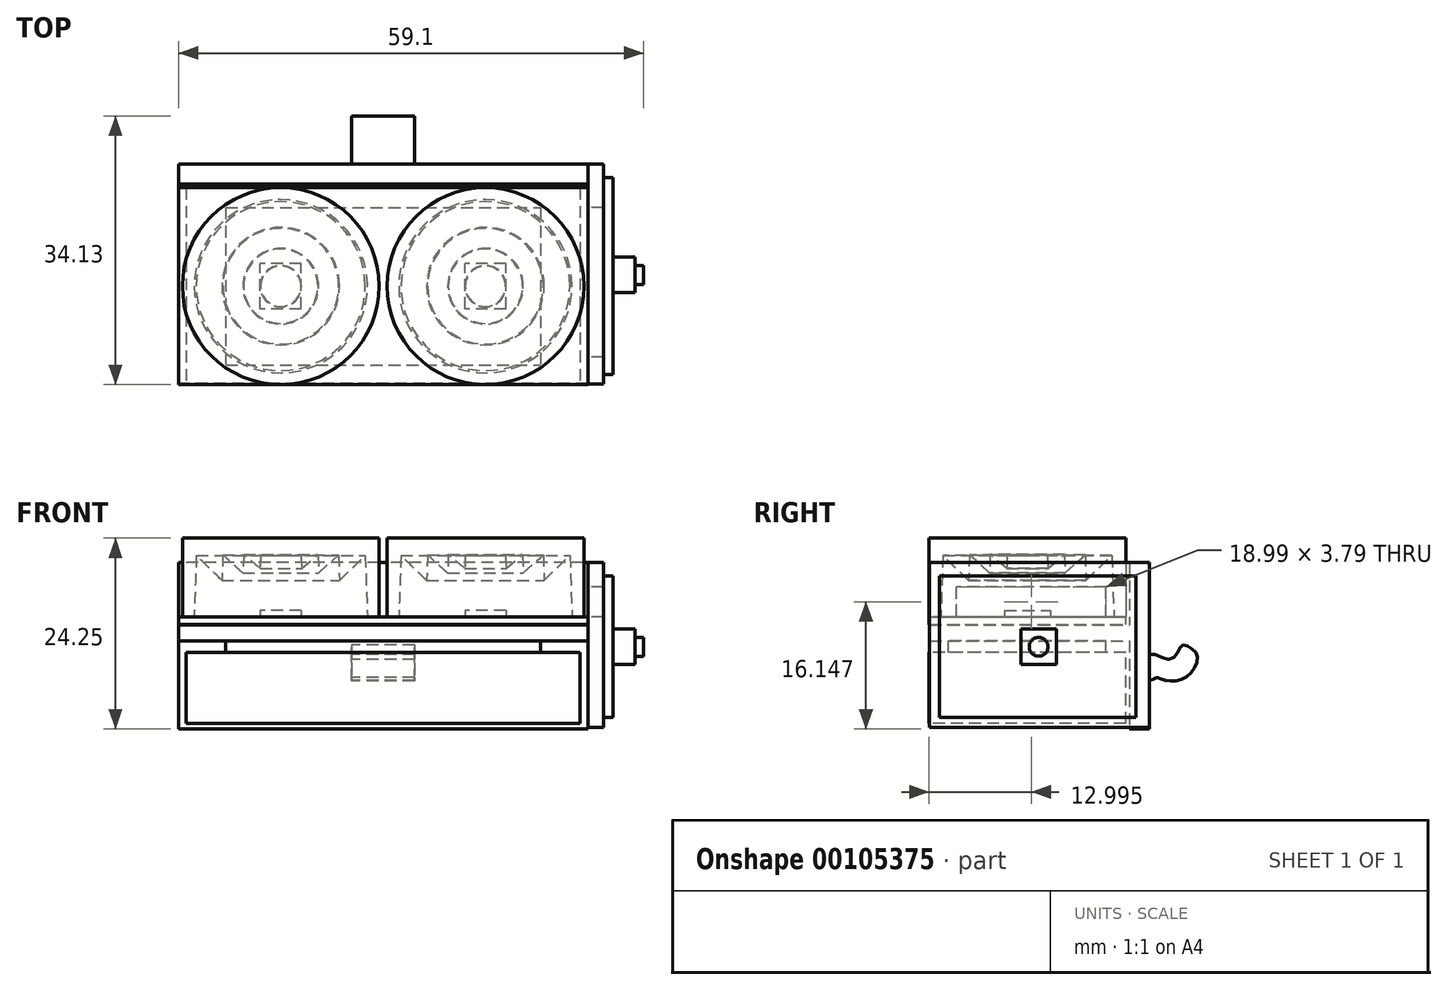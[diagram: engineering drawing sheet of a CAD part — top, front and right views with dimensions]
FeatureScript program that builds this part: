
annotation { "Feature Type Name" : "Feature", "Feature Type Description" : "" }
export const myFeature = defineFeature(function(context is Context, id is Id, definition is map)
    precondition{}
    {
        {
            var Q0;
            Q0=qCreatedBy(makeId("Top.planeOp"),FACE);
            var sketch = newSketch(context, id + "F0", { "sketchPlane" : qUnion([Q0])});
            skLineSegment(sketch, "E0.bottom", {"start": v(26, -12.5) * mm, "end": v(-26, -12.5) * mm});
            skLineSegment(sketch, "E0.top", {"start": v(26, 12.5) * mm, "end": v(-26, 12.5) * mm});
            skLineSegment(sketch, "E0.left", {"start": v(26, -12.5) * mm, "end": v(26, 12.5) * mm});
            skLineSegment(sketch, "E0.right", {"start": v(-26, -12.5) * mm, "end": v(-26, 12.5) * mm});
            skPoint(sketch, "E0.middle", {"position": v(0, 0) * mm});
            skLineSegment(sketch, "E1", {"start": v(-26, 0) * mm, "end": v(26, 0) * mm, "construction": true});
            skLineSegment(sketch, "E2", {"start": v(0, 12.5) * mm, "end": v(0, -12.5) * mm, "construction": true});
            skLineSegment(sketch, "E3", {"start": v(13, 12.5) * mm, "end": v(13, -12.5) * mm, "construction": true});
            skLineSegment(sketch, "E4", {"start": v(-13, 12.5) * mm, "end": v(-13, -12.5) * mm, "construction": true});
            skSolve(sketch);
        }
        {
            var Q0;
            Q0=qCreatedBy(makeId("Front.planeOp"),FACE);
            var sketch = newSketch(context, id + "F1", { "sketchPlane" : qUnion([Q0])});
            skLineSegment(sketch, "E5", {"start": v(13, 0) * mm, "end": v(13, 10) * mm, "construction": true});
            skLineSegment(sketch, "E6", {"start": v(13, 10) * mm, "end": v(25.5, 10) * mm});
            skLineSegment(sketch, "E7", {"start": v(25.5, 10) * mm, "end": v(25.5, 0) * mm});
            skLineSegment(sketch, "E8", {"start": v(25.5, 0) * mm, "end": v(24, 0) * mm});
            skLineSegment(sketch, "E9", {"start": v(24, 0) * mm, "end": v(23.73, 7.79) * mm});
            skLineSegment(sketch, "E10", {"start": v(23.73, 7.79) * mm, "end": v(20.47, 4.62) * mm});
            skLineSegment(sketch, "E11", {"start": v(20.47, 4.62) * mm, "end": v(20.35, 7.89) * mm});
            skLineSegment(sketch, "E12", {"start": v(20.35, 7.89) * mm, "end": v(17.8, 5.54) * mm});
            skLineSegment(sketch, "E13", {"start": v(17.8, 5.54) * mm, "end": v(17.72, 7.9) * mm});
            skLineSegment(sketch, "E14", {"start": v(17.72, 7.9) * mm, "end": v(15.63, 6.16) * mm});
            skLineSegment(sketch, "E15", {"start": v(15.63, 6.16) * mm, "end": v(15.57, 7.82) * mm});
            skLineSegment(sketch, "E16", {"start": v(13, 7.82) * mm, "end": v(13, 10) * mm});
            skLineSegment(sketch, "E17", {"start": v(0, 0) * mm, "end": v(13, 0) * mm, "construction": true});
            skLineSegment(sketch, "E18", {"start": v(15.57, 7.82) * mm, "end": v(13, 7.82) * mm});
            skSolve(sketch);
        }
        {
            var Q0;
            Q0 = qSketchRegion(id + "F1", true);
            var Q1;
            Q1=sQuery(id+"F1.wireOp",EDGE,"E5");
            revolve(context, id + "F2", {"entities" : qUnion([Q0]), "axis" : qUnion([Q1]), "revolveType" : RevolveType.FULL});
        }
        {
            var Q0;
            Q0=qCreatedBy(makeId("Top.planeOp"),FACE);
            var sketch = newSketch(context, id + "F3", { "sketchPlane" : qUnion([Q0])});
            skLineSegment(sketch, "E19.bottom", {"start": v(15.6, -2.9) * mm, "end": v(10.4, -2.9) * mm});
            skLineSegment(sketch, "E19.top", {"start": v(15.6, 2.9) * mm, "end": v(10.4, 2.9) * mm});
            skLineSegment(sketch, "E19.left", {"start": v(15.6, -2.9) * mm, "end": v(15.6, 2.9) * mm});
            skLineSegment(sketch, "E19.right", {"start": v(10.4, -2.9) * mm, "end": v(10.4, 2.9) * mm});
            skPoint(sketch, "E19.middle", {"position": v(13, 0) * mm});
            skSolve(sketch);
        }
        {
            var Q0;
            Q0 = qSketchRegion(id + "F3", true);
            extrude(context, id + "F4", {"entities" : qUnion([Q0]), "depth" : 0.8 * mm});
        }
        {
            var Q0;
            Q0 = qSketchRegion(id + "F0", true);
            extrude(context, id + "F5", {"entities" : qUnion([Q0]), "oppositeDirection" : true, "depth" : 1 * mm});
        }
        {
            var Q0;
            Q0=qCreatedBy(makeId("Right.planeOp"),FACE);
            var sketch = newSketch(context, id + "F6", { "sketchPlane" : qUnion([Q0])});
            skLineSegment(sketch, "E20.bottom", {"start": v(-12.4, -1.05) * mm, "end": v(12.96, -1.05) * mm});
            skLineSegment(sketch, "E20.top", {"start": v(-12.4, -3.05) * mm, "end": v(12.96, -3.05) * mm});
            skLineSegment(sketch, "E20.left", {"start": v(-12.4, -1.05) * mm, "end": v(-12.4, -3.05) * mm});
            skLineSegment(sketch, "E21.bottom", {"start": v(12.96, 6.9) * mm, "end": v(15.52, 6.9) * mm});
            skLineSegment(sketch, "E21.top", {"start": v(12.96, -14.25) * mm, "end": v(15.52, -14.25) * mm});
            skLineSegment(sketch, "E21.left", {"start": v(12.96, 6.9) * mm, "end": v(12.96, -1.05) * mm});
            skLineSegment(sketch, "E21.right", {"start": v(15.52, 6.9) * mm, "end": v(15.52, -4.8) * mm});
            skLineSegment(sketch, "E22.trimOffspring", {"start": v(12.96, -3.05) * mm, "end": v(12.96, -14.25) * mm});
            skFitSpline(sketch, "E23", {"points": [v(15.52, -4.8) * mm, v(17.62, -5.37) * mm, v(19.02, -4.67) * mm, v(19.65, -3.62) * mm, v(20.77, -3.97) * mm, v(21.6, -4.95) * mm, v(21.19, -6.55) * mm, v(19.93, -7.81) * mm, v(18.4, -8.16) * mm, v(17.13, -7.95) * mm, v(16.23, -7.74) * mm, v(15.52, -8.1) * mm, v(15.52, -4.8) * mm]});
            skLineSegment(sketch, "E24.trimOffspring", {"start": v(15.52, -8.1) * mm, "end": v(15.52, -14.25) * mm});
            skSolve(sketch);
        }
        {
            var Q0;
            Q0 = qSketchRegion(id + "F6", true);
            extrude(context, id + "F7", {"entities" : qUnion([Q0]), "endBound" : BoundingType.SYMMETRIC, "depth" : 52 * mm});
        }
        {
            var Q0;
            Q0=makeQuery(id+"F7.opExtrude","SWEPT_FACE",FACE,{"disambiguationData":[OSD([sQuery(id+"F6.wireOp",EDGE,"E21.bottom")])]});
            var sketch = newSketch(context, id + "F8", { "sketchPlane" : qUnion([Q0])});
            skLineSegment(sketch, "E25.bottom", {"start": v(26, 15.52) * mm, "end": v(4, 15.52) * mm});
            skLineSegment(sketch, "E25.top", {"start": v(26, 22.23) * mm, "end": v(4, 22.23) * mm});
            skLineSegment(sketch, "E25.left", {"start": v(26, 15.52) * mm, "end": v(26, 22.23) * mm});
            skLineSegment(sketch, "E25.right", {"start": v(4, 15.52) * mm, "end": v(4, 22.23) * mm});
            skLineSegment(sketch, "E26.bottom", {"start": v(-26, 15.52) * mm, "end": v(-4, 15.52) * mm});
            skLineSegment(sketch, "E26.top", {"start": v(-26, 22.17) * mm, "end": v(-4, 22.17) * mm});
            skLineSegment(sketch, "E26.left", {"start": v(-26, 15.52) * mm, "end": v(-26, 22.17) * mm});
            skLineSegment(sketch, "E26.right", {"start": v(-4, 15.52) * mm, "end": v(-4, 22.17) * mm});
            skSolve(sketch);
        }
        {
            var Q0;
            Q0 = qSketchRegion(id + "F8", true);
            extrude(context, id + "F9", {"entities" : qUnion([Q0]), "operationType" : NewBodyOperationType.REMOVE, "oppositeDirection" : true, "depth" : 25 * mm});
        }
        {
            var Q0;
            Q0=makeQuery(id+"F7.opExtrude","SWEPT_FACE",FACE,{"disambiguationData":[OSD([sQuery(id+"F6.wireOp",EDGE,"E20.top")])]});
            var sketch = newSketch(context, id + "F10", { "sketchPlane" : qUnion([Q0])});
            skLineSegment(sketch, "E27.bottom", {"start": v(-20, -10) * mm, "end": v(20, -10) * mm});
            skLineSegment(sketch, "E27.top", {"start": v(-20, 10) * mm, "end": v(20, 10) * mm});
            skLineSegment(sketch, "E27.left", {"start": v(-20, -10) * mm, "end": v(-20, 10) * mm});
            skLineSegment(sketch, "E27.right", {"start": v(20, -10) * mm, "end": v(20, 10) * mm});
            skPoint(sketch, "E27.middle", {"position": v(0, 0) * mm});
            skSolve(sketch);
        }
        {
            var Q0;
            Q0 = qSketchRegion(id + "F10", true);
            extrude(context, id + "F11", {"entities" : qUnion([Q0]), "depth" : 1.5 * mm});
        }
        {
            var Q0;
            Q0=makeQuery(id+"F11.opExtrude","CAP_FACE",FACE,{"disambiguationData":[OSD([sQuery(id+"F10.wireOp",EDGE,"E27.bottom"),sQuery(id+"F10.wireOp",EDGE,"E27.top"),sQuery(id+"F10.wireOp",EDGE,"E27.left"),sQuery(id+"F10.wireOp",EDGE,"E27.right")])],"isStart":false});
            var sketch = newSketch(context, id + "F12", { "sketchPlane" : qUnion([Q0])});
            skLineSegment(sketch, "E28.bottom", {"start": v(-25, -12.5) * mm, "end": v(25, -12.5) * mm});
            skLineSegment(sketch, "E28.top", {"start": v(-25, 12.5) * mm, "end": v(25, 12.5) * mm});
            skLineSegment(sketch, "E28.left", {"start": v(-25, -12.5) * mm, "end": v(-25, 12.5) * mm});
            skLineSegment(sketch, "E28.right", {"start": v(25, -12.5) * mm, "end": v(25, 12.5) * mm});
            skPoint(sketch, "E28.middle", {"position": v(0, 0) * mm});
            skSolve(sketch);
        }
        {
            var Q0;
            Q0 = qSketchRegion(id + "F12", true);
            extrude(context, id + "F13", {"entities" : qUnion([Q0]), "depth" : 9 * mm});
        }
        {
            var Q0;
            Q0=makeQuery(id+"F7.opExtrude","CAP_FACE",FACE,{"disambiguationData":[OSD([sQuery(id+"F6.wireOp",EDGE,"E20.bottom"),sQuery(id+"F6.wireOp",EDGE,"E20.top"),sQuery(id+"F6.wireOp",EDGE,"E20.left"),sQuery(id+"F6.wireOp",EDGE,"E21.bottom"),sQuery(id+"F6.wireOp",EDGE,"E21.top"),sQuery(id+"F6.wireOp",EDGE,"E21.left"),sQuery(id+"F6.wireOp",EDGE,"E21.right"),sQuery(id+"F6.wireOp",EDGE,"E22.trimOffspring"),sQuery(id+"F6.wireOp",EDGE,"E23"),sQuery(id+"F6.wireOp",EDGE,"E24.trimOffspring")])],"isStart":false});
            var sketch = newSketch(context, id + "F14", { "sketchPlane" : qUnion([Q0])});
            skLineSegment(sketch, "E29.bottom", {"start": v(15.52, 6.9) * mm, "end": v(-12.41, 6.9) * mm});
            skLineSegment(sketch, "E29.top", {"start": v(15.52, -14.05) * mm, "end": v(-12.41, -14.05) * mm});
            skLineSegment(sketch, "E29.left", {"start": v(15.52, 6.9) * mm, "end": v(15.52, -14.05) * mm});
            skLineSegment(sketch, "E29.right", {"start": v(-12.41, 6.9) * mm, "end": v(-12.41, -14.05) * mm});
            skLineSegment(sketch, "E30.bottom", {"start": v(10, 0) * mm, "end": v(-9, 0) * mm});
            skLineSegment(sketch, "E30.top", {"start": v(10, 3.8) * mm, "end": v(-9, 3.8) * mm});
            skLineSegment(sketch, "E30.left", {"start": v(10, 0) * mm, "end": v(10, 3.8) * mm});
            skLineSegment(sketch, "E30.right", {"start": v(-9, 0) * mm, "end": v(-9, 3.8) * mm});
            skSolve(sketch);
        }
        {
            var Q0;
            Q0 = qSketchRegion(id + "F14", true);
            extrude(context, id + "F15", {"entities" : qUnion([Q0]), "depth" : 2 * mm});
        }
        {
            var Q0;
            Q0=makeQuery(id+"F15.opExtrude","CAP_FACE",FACE,{"disambiguationData":[OSD([sQuery(id+"F14.wireOp",EDGE,"E29.bottom"),sQuery(id+"F14.wireOp",EDGE,"E29.top"),sQuery(id+"F14.wireOp",EDGE,"E29.left"),sQuery(id+"F14.wireOp",EDGE,"E29.right"),sQuery(id+"F14.wireOp",EDGE,"E30.bottom"),sQuery(id+"F14.wireOp",EDGE,"E30.top"),sQuery(id+"F14.wireOp",EDGE,"E30.left"),sQuery(id+"F14.wireOp",EDGE,"E30.right")])],"isStart":false});
            var sketch = newSketch(context, id + "F16", { "sketchPlane" : qUnion([Q0])});
            skLineSegment(sketch, "E31.bottom", {"start": v(13.8, 5.2) * mm, "end": v(-11.2, 5.2) * mm});
            skLineSegment(sketch, "E31.top", {"start": v(13.8, -12.8) * mm, "end": v(-11.2, -12.8) * mm});
            skLineSegment(sketch, "E31.left", {"start": v(13.8, 5.2) * mm, "end": v(13.8, -12.8) * mm});
            skLineSegment(sketch, "E31.right", {"start": v(-11.2, 5.2) * mm, "end": v(-11.2, -12.8) * mm});
            skLineSegment(sketch, "E32", {"start": v(13.8, -3.8) * mm, "end": v(-11.2, -3.8) * mm, "construction": true});
            skLineSegment(sketch, "E33", {"start": v(1.3, 5.2) * mm, "end": v(1.56, -12.8) * mm, "construction": true});
            skPoint(sketch, "E33.endSnap0", {"position": v(1.56, 6.9) * mm});
            skSolve(sketch);
        }
        {
            var Q0;
            Q0 = qSketchRegion(id + "F16", true);
            extrude(context, id + "F17", {"entities" : qUnion([Q0]), "depth" : 1.2 * mm});
        }
        {
            var Q0;
            Q0=makeQuery(id+"F17.opExtrude","CAP_FACE",FACE,{"disambiguationData":[OSD([sQuery(id+"F16.wireOp",EDGE,"E31.bottom"),sQuery(id+"F16.wireOp",EDGE,"E31.top"),sQuery(id+"F16.wireOp",EDGE,"E31.left"),sQuery(id+"F16.wireOp",EDGE,"E31.right")])],"isStart":false});
            var sketch = newSketch(context, id + "F18", { "sketchPlane" : qUnion([Q0])});
            skLineSegment(sketch, "E34.bottom", {"start": v(-0.82, -6.06) * mm, "end": v(3.68, -6.06) * mm});
            skLineSegment(sketch, "E34.top", {"start": v(-0.82, -1.56) * mm, "end": v(3.68, -1.56) * mm});
            skLineSegment(sketch, "E34.left", {"start": v(-0.82, -6.06) * mm, "end": v(-0.82, -1.56) * mm});
            skLineSegment(sketch, "E34.right", {"start": v(3.68, -6.06) * mm, "end": v(3.68, -1.56) * mm});
            skPoint(sketch, "E34.middle", {"position": v(1.43, -3.8) * mm});
            skSolve(sketch);
        }
        {
            var Q0;
            Q0 = qSketchRegion(id + "F18", true);
            extrude(context, id + "F19", {"entities" : qUnion([Q0]), "operationType" : NewBodyOperationType.ADD, "depth" : 2.8 * mm});
        }
        {
            var Q0;
            Q0=makeQuery(id+"F19.opExtrude","CAP_FACE",FACE,{"disambiguationData":[OSD([sQuery(id+"F18.wireOp",EDGE,"E34.bottom"),sQuery(id+"F18.wireOp",EDGE,"E34.top"),sQuery(id+"F18.wireOp",EDGE,"E34.left"),sQuery(id+"F18.wireOp",EDGE,"E34.right")])],"isStart":false});
            var sketch = newSketch(context, id + "F20", { "sketchPlane" : qUnion([Q0])});
            skCircle(sketch, "E35", {"center": v(1.43, -3.8) * mm, "radius": 1.2 * mm});
            skPoint(sketch, "E35.centerSnap0", {"position": v(1.43, -6.06) * mm});
            skSolve(sketch);
        }
        {
            var Q0;
            Q0 = qSketchRegion(id + "F20", true);
            extrude(context, id + "F21", {"entities" : qUnion([Q0]), "operationType" : NewBodyOperationType.ADD, "depth" : 1.1 * mm});
        }
        {
            var Q0;
            Q0=makeQuery(id+"F2.opRevolve","SWEPT_BODY",BODY,{"disambiguationData":[OSD([sQuery(id+"F1.wireOp",EDGE,"E6"),sQuery(id+"F1.wireOp",EDGE,"E7"),sQuery(id+"F1.wireOp",EDGE,"E8"),sQuery(id+"F1.wireOp",EDGE,"E9"),sQuery(id+"F1.wireOp",EDGE,"E10"),sQuery(id+"F1.wireOp",EDGE,"E11"),sQuery(id+"F1.wireOp",EDGE,"E12"),sQuery(id+"F1.wireOp",EDGE,"E13"),sQuery(id+"F1.wireOp",EDGE,"E14"),sQuery(id+"F1.wireOp",EDGE,"E15"),sQuery(id+"F1.wireOp",EDGE,"E16"),sQuery(id+"F1.wireOp",EDGE,"E18")])]});
            transform(context, id + "F22", {"entities" : qUnion([Q0]), "transformType" : TransformType.TRANSLATION_3D, "dx" : -26 * mm, "dy" : 0 * mm, "dz" : 0 * mm, "makeCopy" : true});
        }
        {
            var Q0;
            Q0=makeQuery(id+"F4.opExtrude","SWEPT_BODY",BODY,{"disambiguationData":[OSD([sQuery(id+"F3.wireOp",EDGE,"E19.bottom"),sQuery(id+"F3.wireOp",EDGE,"E19.top"),sQuery(id+"F3.wireOp",EDGE,"E19.left"),sQuery(id+"F3.wireOp",EDGE,"E19.right")])]});
            transform(context, id + "F23", {"entities" : qUnion([Q0]), "transformType" : TransformType.TRANSLATION_3D, "dx" : -26 * mm, "dy" : 0 * mm, "dz" : 0 * mm, "makeCopy" : true});
        }
    });
